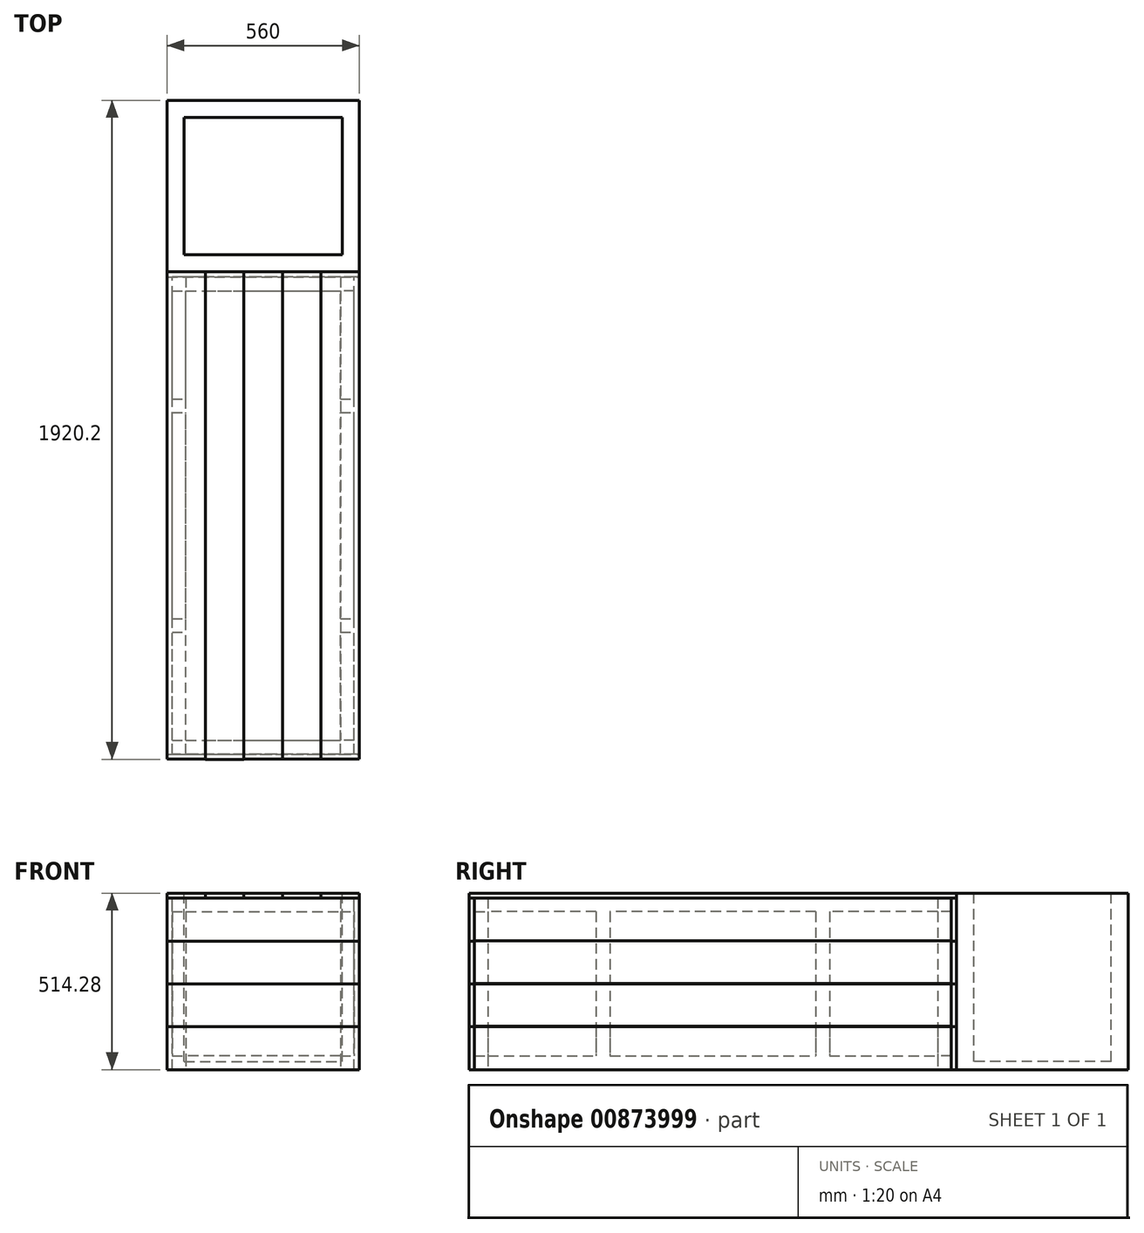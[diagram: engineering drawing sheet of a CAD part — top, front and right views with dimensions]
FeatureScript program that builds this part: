
annotation { "Feature Type Name" : "Feature", "Feature Type Description" : "" }
export const myFeature = defineFeature(function(context is Context, id is Id, definition is map)
    precondition{}
    {
        {
            var Q0;
            Q0=qCreatedBy(makeId("Right.planeOp"),FACE);
            var sketch = newSketch(context, id + "F0", { "sketchPlane" : qUnion([Q0])});
            skLineSegment(sketch, "E0.bottom", {"start": v(0, 0) * mm, "end": v(1390, 0) * mm});
            skLineSegment(sketch, "E0.top", {"start": v(0, 40) * mm, "end": v(1390, 40) * mm});
            skLineSegment(sketch, "E0.left", {"start": v(0, 0) * mm, "end": v(0, 40) * mm});
            skLineSegment(sketch, "E0.right", {"start": v(1390, 0) * mm, "end": v(1390, 40) * mm});
            skSolve(sketch);
        }
        {
            var Q0;
            Q0 = qSketchRegion(id + "F0", true);
            extrude(context, id + "F1", {"entities" : qUnion([Q0]), "depth" : 40 * mm, "offsetDistance" : 25 * mm});
        }
        {
            var Q0;
            Q0=makeQuery(id+"F1.opExtrude","CAP_FACE",FACE,{"disambiguationData":[OSD([sQuery(id+"F0.wireOp",EDGE,"E0.bottom"),sQuery(id+"F0.wireOp",EDGE,"E0.top"),sQuery(id+"F0.wireOp",EDGE,"E0.left"),sQuery(id+"F0.wireOp",EDGE,"E0.right")])],"isStart":true});
            var sketch = newSketch(context, id + "F2", { "sketchPlane" : qUnion([Q0])});
            skLineSegment(sketch, "E1.bottom", {"start": v(-1390, 40) * mm, "end": v(-1350, 40) * mm});
            skLineSegment(sketch, "E1.top", {"start": v(-1390, 0) * mm, "end": v(-1350, 0) * mm});
            skLineSegment(sketch, "E1.left", {"start": v(-1390, 40) * mm, "end": v(-1390, 0) * mm});
            skLineSegment(sketch, "E1.right", {"start": v(-1350, 40) * mm, "end": v(-1350, 0) * mm});
            skLineSegment(sketch, "E2.bottom", {"start": v(0, 40) * mm, "end": v(-40, 40) * mm});
            skLineSegment(sketch, "E2.top", {"start": v(0, 0) * mm, "end": v(-40, 0) * mm});
            skLineSegment(sketch, "E2.left", {"start": v(0, 40) * mm, "end": v(0, 0) * mm});
            skLineSegment(sketch, "E2.right", {"start": v(-40, 40) * mm, "end": v(-40, 0) * mm});
            skSolve(sketch);
        }
        {
            var Q0;
            Q0 = qSketchRegion(id + "F2", true);
            extrude(context, id + "F3", {"entities" : qUnion([Q0]), "operationType" : NewBodyOperationType.ADD, "depth" : 490 * mm, "offsetDistance" : 25 * mm});
        }
        {
            var Q0;
            Q0=makeQuery(id+"F3.opExtrude","SWEPT_FACE",FACE,{"disambiguationData":[OSD([sQuery(id+"F2.wireOp",EDGE,"E1.right")])]});
            var sketch = newSketch(context, id + "F4", { "sketchPlane" : qUnion([Q0])});
            skLineSegment(sketch, "E3.bottom", {"start": v(-490, 40) * mm, "end": v(-450, 40) * mm});
            skLineSegment(sketch, "E3.top", {"start": v(-490, 0) * mm, "end": v(-450, 0) * mm});
            skLineSegment(sketch, "E3.left", {"start": v(-490, 40) * mm, "end": v(-490, 0) * mm});
            skLineSegment(sketch, "E3.right", {"start": v(-450, 40) * mm, "end": v(-450, 0) * mm});
            skSolve(sketch);
        }
        {
            var Q0;
            Q0=makeQuery(id+"F4.imprint","IMPRINT",FACE,{"disambiguationData":[TD([[makeQuery(id+"F4.imprint","IMPRINT",EDGE,{"derivedFrom":sQuery(id+"F4.wireOp",EDGE,"E3.bottom")}),-1.0]])]});
            extrude(context, id + "F5", {"entities" : qUnion([Q0]), "operationType" : NewBodyOperationType.ADD, "depth" : 1310 * mm, "offsetDistance" : 25 * mm});
        }
        {
            var Q0;
            Q0=makeQuery(id+"F5.boolean.opBoolean","MERGE",FACE,{"derivedFrom":[makeQuery(id+"F3.boolean.opBoolean","MERGE",FACE,{"derivedFrom":[makeQuery(id+"F1.opExtrude","SWEPT_FACE",FACE,{"disambiguationData":[OSD([sQuery(id+"F0.wireOp",EDGE,"E0.top")])]}),makeQuery(id+"F3.opExtrude","SWEPT_FACE",FACE,{"disambiguationData":[OSD([sQuery(id+"F2.wireOp",EDGE,"E1.bottom")])]}),makeQuery(id+"F3.opExtrude","SWEPT_FACE",FACE,{"disambiguationData":[OSD([sQuery(id+"F2.wireOp",EDGE,"E2.bottom")])]})]}),makeQuery(id+"F5.opExtrude","SWEPT_FACE",FACE,{"disambiguationData":[OSD([sQuery(id+"F4.wireOp",EDGE,"E3.bottom")])]})]});
            var sketch = newSketch(context, id + "F6", { "sketchPlane" : qUnion([Q0])});
            skLineSegment(sketch, "E4.bottom", {"start": v(-490, 1390) * mm, "end": v(-450, 1390) * mm});
            skLineSegment(sketch, "E4.top", {"start": v(-490, 1350) * mm, "end": v(-450, 1350) * mm});
            skLineSegment(sketch, "E4.left", {"start": v(-490, 1390) * mm, "end": v(-490, 1350) * mm});
            skLineSegment(sketch, "E4.right", {"start": v(-450, 1390) * mm, "end": v(-450, 1350) * mm});
            skLineSegment(sketch, "E5.bottom", {"start": v(40, 1390) * mm, "end": v(0, 1390) * mm});
            skLineSegment(sketch, "E5.top", {"start": v(40, 1350) * mm, "end": v(0, 1350) * mm});
            skLineSegment(sketch, "E5.left", {"start": v(40, 1390) * mm, "end": v(40, 1350) * mm});
            skLineSegment(sketch, "E5.right", {"start": v(0, 1390) * mm, "end": v(0, 1350) * mm});
            skLineSegment(sketch, "E6.bottom", {"start": v(40, 0) * mm, "end": v(0, 0) * mm});
            skLineSegment(sketch, "E6.top", {"start": v(40, 40) * mm, "end": v(0, 40) * mm});
            skLineSegment(sketch, "E6.left", {"start": v(40, 0) * mm, "end": v(40, 40) * mm});
            skLineSegment(sketch, "E6.right", {"start": v(0, 0) * mm, "end": v(0, 40) * mm});
            skLineSegment(sketch, "E7.bottom", {"start": v(-490, 0) * mm, "end": v(-450, 0) * mm});
            skLineSegment(sketch, "E7.top", {"start": v(-490, 40) * mm, "end": v(-450, 40) * mm});
            skLineSegment(sketch, "E7.left", {"start": v(-490, 0) * mm, "end": v(-490, 40) * mm});
            skLineSegment(sketch, "E7.right", {"start": v(-450, 0) * mm, "end": v(-450, 40) * mm});
            skSolve(sketch);
        }
        {
            var Q0;
            Q0 = qSketchRegion(id + "F6", true);
            extrude(context, id + "F7", {"entities" : qUnion([Q0]), "operationType" : NewBodyOperationType.ADD, "depth" : 420 * mm, "offsetDistance" : 25 * mm});
        }
        {
            var Q0;
            Q0=makeQuery(id+"F7.opExtrude","CAP_FACE",FACE,{"disambiguationData":[OSD([sQuery(id+"F6.wireOp",EDGE,"E4.bottom"),sQuery(id+"F6.wireOp",EDGE,"E4.top"),sQuery(id+"F6.wireOp",EDGE,"E4.left"),sQuery(id+"F6.wireOp",EDGE,"E4.right")])],"isStart":false});
            var sketch = newSketch(context, id + "F8", { "sketchPlane" : qUnion([Q0])});
            skLineSegment(sketch, "E8.bottom", {"start": v(-490, 1390) * mm, "end": v(40, 1390) * mm});
            skLineSegment(sketch, "E8.top", {"start": v(-490, 0) * mm, "end": v(40, 0) * mm});
            skLineSegment(sketch, "E8.left", {"start": v(-490, 1390) * mm, "end": v(-490, 0) * mm});
            skLineSegment(sketch, "E8.right", {"start": v(40, 1390) * mm, "end": v(40, 0) * mm});
            skLineSegment(sketch, "E9.bottom", {"start": v(-450, 1350) * mm, "end": v(0, 1350) * mm});
            skLineSegment(sketch, "E9.top", {"start": v(-450, 40) * mm, "end": v(0, 40) * mm});
            skLineSegment(sketch, "E9.left", {"start": v(-450, 1350) * mm, "end": v(-450, 40) * mm});
            skLineSegment(sketch, "E9.right", {"start": v(0, 1350) * mm, "end": v(0, 40) * mm});
            skSolve(sketch);
        }
        {
            var Q0;
            Q0 = qSketchRegion(id + "F8", true);
            extrude(context, id + "F9", {"entities" : qUnion([Q0]), "operationType" : NewBodyOperationType.ADD, "depth" : 40 * mm, "offsetDistance" : 25 * mm});
        }
        {
            var Q0;
            {var subQ1=sQuery(id+"F2.wireOp",EDGE,"E2.bottom");var subQ2=makeQuery(id+"F3.opExtrude","SWEPT_FACE",FACE,{"disambiguationData":[OSD([subQ1])]});var subQ3=sQuery(id+"F2.wireOp",EDGE,"E1.bottom");var subQ4=makeQuery(id+"F3.opExtrude","SWEPT_FACE",FACE,{"disambiguationData":[OSD([subQ3])]});var subQ5=makeQuery(id+"F5.opExtrude","SWEPT_FACE",FACE,{"disambiguationData":[OSD([sQuery(id+"F4.wireOp",EDGE,"E3.bottom")])]});var subQ7=makeQuery(id+"F1.opExtrude","SWEPT_FACE",FACE,{"disambiguationData":[OSD([sQuery(id+"F0.wireOp",EDGE,"E0.top")])]});Q0=makeQuery(id+"F7.boolean.opBoolean","SPLIT",FACE,{"disambiguationData":[TD([makeQuery(id+"F5.opExtrude","SWEPT_FACE",FACE,{"disambiguationData":[OSD([sQuery(id+"F4.wireOp",EDGE,"E3.left")])]})])],"derivedFrom":makeQuery(id+"F5.boolean.opBoolean","MERGE",FACE,{"derivedFrom":[makeQuery(id+"F3.boolean.opBoolean","MERGE",FACE,{"derivedFrom":[subQ7,subQ4,subQ2]}),subQ5]})});}
            var sketch = newSketch(context, id + "F10", { "sketchPlane" : qUnion([Q0])});
            skLineSegment(sketch, "E10", {"start": v(-490, 695) * mm, "end": v(200.64, 695) * mm, "construction": true});
            skLineSegment(sketch, "E11.bottom", {"start": v(-490, 1035) * mm, "end": v(-450, 1035) * mm});
            skLineSegment(sketch, "E11.top", {"start": v(-490, 995) * mm, "end": v(-450, 995) * mm});
            skLineSegment(sketch, "E11.left", {"start": v(-490, 1035) * mm, "end": v(-490, 995) * mm});
            skLineSegment(sketch, "E11.right", {"start": v(-450, 1035) * mm, "end": v(-450, 995) * mm});
            skLineSegment(sketch, "E12.bottom", {"start": v(-490, 395) * mm, "end": v(-450, 395) * mm});
            skLineSegment(sketch, "E12.top", {"start": v(-490, 355) * mm, "end": v(-450, 355) * mm});
            skLineSegment(sketch, "E12.left", {"start": v(-490, 395) * mm, "end": v(-490, 355) * mm});
            skLineSegment(sketch, "E12.right", {"start": v(-450, 395) * mm, "end": v(-450, 355) * mm});
            skSolve(sketch);
        }
        {
            var Q0;
            Q0 = qSketchRegion(id + "F10", true);
            extrude(context, id + "F11", {"entities" : qUnion([Q0]), "operationType" : NewBodyOperationType.ADD, "depth" : 420 * mm, "offsetDistance" : 25 * mm});
        }
        {
            var Q0;
            {var subQ0=makeQuery(id+"F5.opExtrude","SWEPT_FACE",FACE,{"disambiguationData":[OSD([sQuery(id+"F4.wireOp",EDGE,"E3.bottom")])]});var subQ1=makeQuery(id+"F3.opExtrude","SWEPT_FACE",FACE,{"disambiguationData":[OSD([sQuery(id+"F2.wireOp",EDGE,"E2.bottom")])]});var subQ4=sQuery(id+"F0.wireOp",EDGE,"E0.top");var subQ6=makeQuery(id+"F1.opExtrude","SWEPT_FACE",FACE,{"disambiguationData":[OSD([subQ4])]});var subQ7=makeQuery(id+"F3.opExtrude","SWEPT_FACE",FACE,{"disambiguationData":[OSD([sQuery(id+"F2.wireOp",EDGE,"E1.bottom")])]});Q0=makeQuery(id+"F7.boolean.opBoolean","SPLIT",FACE,{"disambiguationData":[TD([makeQuery(id+"F7.opExtrude","SWEPT_FACE",FACE,{"disambiguationData":[OSD([sQuery(id+"F6.wireOp",EDGE,"E5.left")])]})])],"derivedFrom":makeQuery(id+"F5.boolean.opBoolean","MERGE",FACE,{"derivedFrom":[makeQuery(id+"F3.boolean.opBoolean","MERGE",FACE,{"derivedFrom":[subQ6,subQ7,subQ1]}),subQ0]})});}
            var sketch = newSketch(context, id + "F12", { "sketchPlane" : qUnion([Q0])});
            skLineSegment(sketch, "E13", {"start": v(40, 695) * mm, "end": v(-725.04, 695) * mm, "construction": true});
            skLineSegment(sketch, "E14.bottom", {"start": v(0, 1035) * mm, "end": v(40, 1035) * mm});
            skLineSegment(sketch, "E14.top", {"start": v(0, 995) * mm, "end": v(40, 995) * mm});
            skLineSegment(sketch, "E14.left", {"start": v(0, 1035) * mm, "end": v(0, 995) * mm});
            skLineSegment(sketch, "E14.right", {"start": v(40, 1035) * mm, "end": v(40, 995) * mm});
            skLineSegment(sketch, "E15.bottom", {"start": v(0, 395) * mm, "end": v(40, 395) * mm});
            skLineSegment(sketch, "E15.top", {"start": v(0, 355) * mm, "end": v(40, 355) * mm});
            skLineSegment(sketch, "E15.left", {"start": v(0, 395) * mm, "end": v(0, 355) * mm});
            skLineSegment(sketch, "E15.right", {"start": v(40, 395) * mm, "end": v(40, 355) * mm});
            skSolve(sketch);
        }
        {
            var Q0;
            Q0 = qSketchRegion(id + "F12", true);
            extrude(context, id + "F13", {"entities" : qUnion([Q0]), "operationType" : NewBodyOperationType.ADD, "depth" : 420 * mm, "offsetDistance" : 25 * mm});
        }
        {
            var Q0;
            Q0=makeQuery(id+"F11.boolean.opBoolean","MERGE",FACE,{"derivedFrom":[makeQuery(id+"F9.boolean.opBoolean","MERGE",FACE,{"derivedFrom":[makeQuery(id+"F7.boolean.opBoolean","MERGE",FACE,{"derivedFrom":[makeQuery(id+"F5.boolean.opBoolean","MERGE",FACE,{"derivedFrom":[makeQuery(id+"F3.opExtrude","CAP_FACE",FACE,{"disambiguationData":[OSD([sQuery(id+"F2.wireOp",EDGE,"E1.bottom"),sQuery(id+"F2.wireOp",EDGE,"E1.top"),sQuery(id+"F2.wireOp",EDGE,"E1.left"),sQuery(id+"F2.wireOp",EDGE,"E1.right")])],"isStart":false}),makeQuery(id+"F3.opExtrude","CAP_FACE",FACE,{"disambiguationData":[OSD([sQuery(id+"F2.wireOp",EDGE,"E2.bottom"),sQuery(id+"F2.wireOp",EDGE,"E2.top"),sQuery(id+"F2.wireOp",EDGE,"E2.left"),sQuery(id+"F2.wireOp",EDGE,"E2.right")])],"isStart":false}),makeQuery(id+"F5.opExtrude","SWEPT_FACE",FACE,{"disambiguationData":[OSD([sQuery(id+"F4.wireOp",EDGE,"E3.left")])]})]}),makeQuery(id+"F7.opExtrude","SWEPT_FACE",FACE,{"disambiguationData":[OSD([sQuery(id+"F6.wireOp",EDGE,"E4.left")])]}),makeQuery(id+"F7.opExtrude","SWEPT_FACE",FACE,{"disambiguationData":[OSD([sQuery(id+"F6.wireOp",EDGE,"E7.left")])]})]}),makeQuery(id+"F9.opExtrude","SWEPT_FACE",FACE,{"disambiguationData":[OSD([sQuery(id+"F8.wireOp",EDGE,"E8.left")])]})]}),makeQuery(id+"F11.opExtrude","SWEPT_FACE",FACE,{"disambiguationData":[OSD([sQuery(id+"F10.wireOp",EDGE,"E11.left")])]}),makeQuery(id+"F11.opExtrude","SWEPT_FACE",FACE,{"disambiguationData":[OSD([sQuery(id+"F10.wireOp",EDGE,"E12.left")])]})]});
            var sketch = newSketch(context, id + "F14", { "sketchPlane" : qUnion([Q0])});
            skSolve(sketch);
        }
        {
            var Q0;
            Q0=makeQuery(id+"F13.boolean.opBoolean","MERGE",FACE,{"derivedFrom":[makeQuery(id+"F9.boolean.opBoolean","MERGE",FACE,{"derivedFrom":[makeQuery(id+"F7.boolean.opBoolean","MERGE",FACE,{"derivedFrom":[makeQuery(id+"F1.opExtrude","CAP_FACE",FACE,{"disambiguationData":[OSD([sQuery(id+"F0.wireOp",EDGE,"E0.bottom"),sQuery(id+"F0.wireOp",EDGE,"E0.top"),sQuery(id+"F0.wireOp",EDGE,"E0.left"),sQuery(id+"F0.wireOp",EDGE,"E0.right")])],"isStart":false}),makeQuery(id+"F7.opExtrude","SWEPT_FACE",FACE,{"disambiguationData":[OSD([sQuery(id+"F6.wireOp",EDGE,"E5.left")])]}),makeQuery(id+"F7.opExtrude","SWEPT_FACE",FACE,{"disambiguationData":[OSD([sQuery(id+"F6.wireOp",EDGE,"E6.left")])]})]}),makeQuery(id+"F9.opExtrude","SWEPT_FACE",FACE,{"disambiguationData":[OSD([sQuery(id+"F8.wireOp",EDGE,"E8.right")])]})]}),makeQuery(id+"F13.opExtrude","SWEPT_FACE",FACE,{"disambiguationData":[OSD([sQuery(id+"F12.wireOp",EDGE,"E14.right")])]}),makeQuery(id+"F13.opExtrude","SWEPT_FACE",FACE,{"disambiguationData":[OSD([sQuery(id+"F12.wireOp",EDGE,"E15.right")])]})]});
            var sketch = newSketch(context, id + "F15", { "sketchPlane" : qUnion([Q0])});
            skLineSegment(sketch, "E16.bottom", {"start": v(0, 500) * mm, "end": v(1390, 500) * mm});
            skLineSegment(sketch, "E16.top", {"start": v(0, 375) * mm, "end": v(1390, 375) * mm});
            skLineSegment(sketch, "E16.left", {"start": v(0, 500) * mm, "end": v(0, 375) * mm});
            skLineSegment(sketch, "E16.right", {"start": v(1390, 500) * mm, "end": v(1390, 375) * mm});
            skSolve(sketch);
        }
        {
            var Q0;
            Q0 = qSketchRegion(id + "F15", true);
            extrude(context, id + "F16", {"entities" : qUnion([Q0]), "depth" : 15 * mm, "offsetDistance" : 25 * mm});
        }
        {
            var Q0;
            Q0=makeQuery(id+"F13.boolean.opBoolean","MERGE",FACE,{"derivedFrom":[makeQuery(id+"F9.boolean.opBoolean","MERGE",FACE,{"derivedFrom":[makeQuery(id+"F7.boolean.opBoolean","MERGE",FACE,{"derivedFrom":[makeQuery(id+"F1.opExtrude","CAP_FACE",FACE,{"disambiguationData":[OSD([sQuery(id+"F0.wireOp",EDGE,"E0.bottom"),sQuery(id+"F0.wireOp",EDGE,"E0.top"),sQuery(id+"F0.wireOp",EDGE,"E0.left"),sQuery(id+"F0.wireOp",EDGE,"E0.right")])],"isStart":false}),makeQuery(id+"F7.opExtrude","SWEPT_FACE",FACE,{"disambiguationData":[OSD([sQuery(id+"F6.wireOp",EDGE,"E5.left")])]}),makeQuery(id+"F7.opExtrude","SWEPT_FACE",FACE,{"disambiguationData":[OSD([sQuery(id+"F6.wireOp",EDGE,"E6.left")])]})]}),makeQuery(id+"F9.opExtrude","SWEPT_FACE",FACE,{"disambiguationData":[OSD([sQuery(id+"F8.wireOp",EDGE,"E8.right")])]})]}),makeQuery(id+"F13.opExtrude","SWEPT_FACE",FACE,{"disambiguationData":[OSD([sQuery(id+"F12.wireOp",EDGE,"E14.right")])]}),makeQuery(id+"F13.opExtrude","SWEPT_FACE",FACE,{"disambiguationData":[OSD([sQuery(id+"F12.wireOp",EDGE,"E15.right")])]})]});
            var sketch = newSketch(context, id + "F17", { "sketchPlane" : qUnion([Q0])});
            skLineSegment(sketch, "E17.bottom", {"start": v(0, 0) * mm, "end": v(1390, 0) * mm});
            skLineSegment(sketch, "E17.top", {"start": v(0, 125) * mm, "end": v(1390, 125) * mm});
            skLineSegment(sketch, "E17.left", {"start": v(0, 0) * mm, "end": v(0, 125) * mm});
            skLineSegment(sketch, "E17.right", {"start": v(1390, 0) * mm, "end": v(1390, 125) * mm});
            skSolve(sketch);
        }
        {
            var Q0;
            Q0 = qSketchRegion(id + "F17", true);
            extrude(context, id + "F18", {"entities" : qUnion([Q0]), "depth" : 15 * mm, "offsetDistance" : 25 * mm});
        }
        {
            var Q0;
            Q0=makeQuery(id+"F13.boolean.opBoolean","MERGE",FACE,{"derivedFrom":[makeQuery(id+"F9.boolean.opBoolean","MERGE",FACE,{"derivedFrom":[makeQuery(id+"F7.boolean.opBoolean","MERGE",FACE,{"derivedFrom":[makeQuery(id+"F1.opExtrude","CAP_FACE",FACE,{"disambiguationData":[OSD([sQuery(id+"F0.wireOp",EDGE,"E0.bottom"),sQuery(id+"F0.wireOp",EDGE,"E0.top"),sQuery(id+"F0.wireOp",EDGE,"E0.left"),sQuery(id+"F0.wireOp",EDGE,"E0.right")])],"isStart":false}),makeQuery(id+"F7.opExtrude","SWEPT_FACE",FACE,{"disambiguationData":[OSD([sQuery(id+"F6.wireOp",EDGE,"E5.left")])]}),makeQuery(id+"F7.opExtrude","SWEPT_FACE",FACE,{"disambiguationData":[OSD([sQuery(id+"F6.wireOp",EDGE,"E6.left")])]})]}),makeQuery(id+"F9.opExtrude","SWEPT_FACE",FACE,{"disambiguationData":[OSD([sQuery(id+"F8.wireOp",EDGE,"E8.right")])]})]}),makeQuery(id+"F13.opExtrude","SWEPT_FACE",FACE,{"disambiguationData":[OSD([sQuery(id+"F12.wireOp",EDGE,"E14.right")])]}),makeQuery(id+"F13.opExtrude","SWEPT_FACE",FACE,{"disambiguationData":[OSD([sQuery(id+"F12.wireOp",EDGE,"E15.right")])]})]});
            var sketch = newSketch(context, id + "F19", { "sketchPlane" : qUnion([Q0])});
            skLineSegment(sketch, "E18.bottom", {"start": v(0, 251.2) * mm, "end": v(1390, 251.2) * mm});
            skLineSegment(sketch, "E18.top", {"start": v(0, 126.2) * mm, "end": v(1390, 126.2) * mm});
            skLineSegment(sketch, "E18.left", {"start": v(0, 251.2) * mm, "end": v(0, 126.2) * mm});
            skLineSegment(sketch, "E18.right", {"start": v(1390, 251.2) * mm, "end": v(1390, 126.2) * mm});
            skSolve(sketch);
        }
        {
            var Q0;
            Q0 = qSketchRegion(id + "F19", true);
            extrude(context, id + "F20", {"entities" : qUnion([Q0]), "depth" : 15 * mm, "offsetDistance" : 25 * mm});
        }
        {
            var Q0;
            Q0=makeQuery(id+"F13.boolean.opBoolean","MERGE",FACE,{"derivedFrom":[makeQuery(id+"F9.boolean.opBoolean","MERGE",FACE,{"derivedFrom":[makeQuery(id+"F7.boolean.opBoolean","MERGE",FACE,{"derivedFrom":[makeQuery(id+"F1.opExtrude","CAP_FACE",FACE,{"disambiguationData":[OSD([sQuery(id+"F0.wireOp",EDGE,"E0.bottom"),sQuery(id+"F0.wireOp",EDGE,"E0.top"),sQuery(id+"F0.wireOp",EDGE,"E0.left"),sQuery(id+"F0.wireOp",EDGE,"E0.right")])],"isStart":false}),makeQuery(id+"F7.opExtrude","SWEPT_FACE",FACE,{"disambiguationData":[OSD([sQuery(id+"F6.wireOp",EDGE,"E5.left")])]}),makeQuery(id+"F7.opExtrude","SWEPT_FACE",FACE,{"disambiguationData":[OSD([sQuery(id+"F6.wireOp",EDGE,"E6.left")])]})]}),makeQuery(id+"F9.opExtrude","SWEPT_FACE",FACE,{"disambiguationData":[OSD([sQuery(id+"F8.wireOp",EDGE,"E8.right")])]})]}),makeQuery(id+"F13.opExtrude","SWEPT_FACE",FACE,{"disambiguationData":[OSD([sQuery(id+"F12.wireOp",EDGE,"E14.right")])]}),makeQuery(id+"F13.opExtrude","SWEPT_FACE",FACE,{"disambiguationData":[OSD([sQuery(id+"F12.wireOp",EDGE,"E15.right")])]})]});
            var sketch = newSketch(context, id + "F21", { "sketchPlane" : qUnion([Q0])});
            skLineSegment(sketch, "E19.bottom", {"start": v(0, 250) * mm, "end": v(1390, 250) * mm});
            skLineSegment(sketch, "E19.top", {"start": v(0, 375) * mm, "end": v(1390, 375) * mm});
            skLineSegment(sketch, "E19.left", {"start": v(0, 250) * mm, "end": v(0, 375) * mm});
            skLineSegment(sketch, "E19.right", {"start": v(1390, 250) * mm, "end": v(1390, 375) * mm});
            skSolve(sketch);
        }
        {
            var Q0;
            Q0 = qSketchRegion(id + "F21", true);
            extrude(context, id + "F22", {"entities" : qUnion([Q0]), "depth" : 15 * mm, "offsetDistance" : 25 * mm});
        }
        {
            var Q0;
            {var subQ10=sQuery(id+"F8.wireOp",EDGE,"E8.left");Q0=makeQuery(id+"F14.imprint","IMPRINT",FACE,{"disambiguationData":[TD([[makeQuery(id+"F14.imprint","IMPRINT",EDGE,{"derivedFrom":makeQuery(id+"F9.opExtrude","CAP_EDGE",EDGE,{"disambiguationData":[OSD([subQ10])],"isStart":false})}),1.0]])]});}
            var sketch = newSketch(context, id + "F23", { "sketchPlane" : qUnion([Q0])});
            skLineSegment(sketch, "E20.bottom", {"start": v(0, 0) * mm, "end": v(-1390, 0) * mm});
            skLineSegment(sketch, "E20.top", {"start": v(0, 125) * mm, "end": v(-1390, 125) * mm});
            skLineSegment(sketch, "E20.left", {"start": v(0, 0) * mm, "end": v(0, 125) * mm});
            skLineSegment(sketch, "E20.right", {"start": v(-1390, 0) * mm, "end": v(-1390, 125) * mm});
            skSolve(sketch);
        }
        {
            var Q0;
            Q0 = qSketchRegion(id + "F23", true);
            extrude(context, id + "F24", {"entities" : qUnion([Q0]), "depth" : 15 * mm, "offsetDistance" : 25 * mm});
        }
        {
            var Q0;
            {var subQ10=sQuery(id+"F8.wireOp",EDGE,"E8.left");Q0=makeQuery(id+"F14.imprint","IMPRINT",FACE,{"disambiguationData":[TD([[makeQuery(id+"F14.imprint","IMPRINT",EDGE,{"derivedFrom":makeQuery(id+"F9.opExtrude","CAP_EDGE",EDGE,{"disambiguationData":[OSD([subQ10])],"isStart":false})}),1.0]])]});}
            var sketch = newSketch(context, id + "F25", { "sketchPlane" : qUnion([Q0])});
            skLineSegment(sketch, "E21.bottom", {"start": v(0, 124.95) * mm, "end": v(-1390, 124.95) * mm});
            skLineSegment(sketch, "E21.top", {"start": v(0, 250) * mm, "end": v(-1390, 250) * mm});
            skLineSegment(sketch, "E21.left", {"start": v(0, 124.95) * mm, "end": v(0, 250) * mm});
            skLineSegment(sketch, "E21.right", {"start": v(-1390, 124.95) * mm, "end": v(-1390, 250) * mm});
            skSolve(sketch);
        }
        {
            var Q0;
            Q0 = qSketchRegion(id + "F25", true);
            extrude(context, id + "F26", {"entities" : qUnion([Q0]), "depth" : 15 * mm, "offsetDistance" : 25 * mm});
        }
        {
            var Q0;
            {var subQ10=sQuery(id+"F8.wireOp",EDGE,"E8.left");Q0=makeQuery(id+"F14.imprint","IMPRINT",FACE,{"disambiguationData":[TD([[makeQuery(id+"F14.imprint","IMPRINT",EDGE,{"derivedFrom":makeQuery(id+"F9.opExtrude","CAP_EDGE",EDGE,{"disambiguationData":[OSD([subQ10])],"isStart":false})}),1.0]])]});}
            var sketch = newSketch(context, id + "F27", { "sketchPlane" : qUnion([Q0])});
            skLineSegment(sketch, "E22.bottom", {"start": v(0, 249.73) * mm, "end": v(-1390, 249.73) * mm});
            skLineSegment(sketch, "E22.top", {"start": v(0, 374.73) * mm, "end": v(-1390, 374.73) * mm});
            skLineSegment(sketch, "E22.left", {"start": v(0, 249.73) * mm, "end": v(0, 374.73) * mm});
            skLineSegment(sketch, "E22.right", {"start": v(-1390, 249.73) * mm, "end": v(-1390, 374.73) * mm});
            skSolve(sketch);
        }
        {
            var Q0;
            Q0 = qSketchRegion(id + "F27", true);
            extrude(context, id + "F28", {"entities" : qUnion([Q0]), "depth" : 15 * mm, "offsetDistance" : 25 * mm});
        }
        {
            var Q0;
            {var subQ10=sQuery(id+"F8.wireOp",EDGE,"E8.left");Q0=makeQuery(id+"F14.imprint","IMPRINT",FACE,{"disambiguationData":[TD([[makeQuery(id+"F14.imprint","IMPRINT",EDGE,{"derivedFrom":makeQuery(id+"F9.opExtrude","CAP_EDGE",EDGE,{"disambiguationData":[OSD([subQ10])],"isStart":false})}),1.0]])]});}
            var sketch = newSketch(context, id + "F29", { "sketchPlane" : qUnion([Q0])});
            skLineSegment(sketch, "E23.bottom", {"start": v(0, 374.28) * mm, "end": v(-1390, 374.28) * mm});
            skLineSegment(sketch, "E23.top", {"start": v(0, 499.28) * mm, "end": v(-1390, 499.28) * mm});
            skLineSegment(sketch, "E23.left", {"start": v(0, 374.28) * mm, "end": v(0, 499.28) * mm});
            skLineSegment(sketch, "E23.right", {"start": v(-1390, 374.28) * mm, "end": v(-1390, 499.28) * mm});
            skSolve(sketch);
        }
        {
            var Q0;
            Q0 = qSketchRegion(id + "F29", true);
            extrude(context, id + "F30", {"entities" : qUnion([Q0]), "depth" : 15 * mm, "offsetDistance" : 25 * mm});
        }
        {
            var Q0;
            Q0=makeQuery(id+"F9.boolean.opBoolean","MERGE",FACE,{"derivedFrom":[makeQuery(id+"F7.boolean.opBoolean","MERGE",FACE,{"derivedFrom":[makeQuery(id+"F3.boolean.opBoolean","MERGE",FACE,{"derivedFrom":[makeQuery(id+"F1.opExtrude","SWEPT_FACE",FACE,{"disambiguationData":[OSD([sQuery(id+"F0.wireOp",EDGE,"E0.left")])]}),makeQuery(id+"F3.opExtrude","SWEPT_FACE",FACE,{"disambiguationData":[OSD([sQuery(id+"F2.wireOp",EDGE,"E2.left")])]})]}),makeQuery(id+"F7.opExtrude","SWEPT_FACE",FACE,{"disambiguationData":[OSD([sQuery(id+"F6.wireOp",EDGE,"E6.bottom")])]}),makeQuery(id+"F7.opExtrude","SWEPT_FACE",FACE,{"disambiguationData":[OSD([sQuery(id+"F6.wireOp",EDGE,"E7.bottom")])]})]}),makeQuery(id+"F9.opExtrude","SWEPT_FACE",FACE,{"disambiguationData":[OSD([sQuery(id+"F8.wireOp",EDGE,"E8.top")])]})]});
            cPlane(context, id + "F31", {"entities" : qUnion([Q0]), "cplaneType" : CPlaneType.OFFSET, "offset" : 695 * mm, "oppositeDirection" : true, "width" : 150 * mm, "height" : 150 * mm});
        }
        {
            var Q0;
            Q0=makeQuery(id+"F24.opExtrude","SWEPT_FACE",FACE,{"disambiguationData":[OSD([sQuery(id+"F23.wireOp",EDGE,"E20.left")])]});
            var sketch = newSketch(context, id + "F32", { "sketchPlane" : qUnion([Q0])});
            skLineSegment(sketch, "E24.bottom", {"start": v(-505, 0) * mm, "end": v(55, 0) * mm});
            skLineSegment(sketch, "E24.top", {"start": v(-505, 125) * mm, "end": v(55, 125) * mm});
            skLineSegment(sketch, "E24.left", {"start": v(-505, 0) * mm, "end": v(-505, 125) * mm});
            skLineSegment(sketch, "E24.right", {"start": v(55, 0) * mm, "end": v(55, 125) * mm});
            skSolve(sketch);
        }
        {
            var Q0;
            Q0 = qSketchRegion(id + "F32", true);
            extrude(context, id + "F33", {"entities" : qUnion([Q0]), "depth" : 15 * mm, "offsetDistance" : 25 * mm});
        }
        {
            var Q0;
            Q0=makeQuery(id+"F26.opExtrude","SWEPT_FACE",FACE,{"disambiguationData":[OSD([sQuery(id+"F25.wireOp",EDGE,"E21.left")])]});
            var sketch = newSketch(context, id + "F34", { "sketchPlane" : qUnion([Q0])});
            skLineSegment(sketch, "E25.bottom", {"start": v(-505, 124.95) * mm, "end": v(55, 124.95) * mm});
            skLineSegment(sketch, "E25.top", {"start": v(-505, 249.95) * mm, "end": v(55, 249.95) * mm});
            skLineSegment(sketch, "E25.left", {"start": v(-505, 124.95) * mm, "end": v(-505, 249.95) * mm});
            skLineSegment(sketch, "E25.right", {"start": v(55, 124.95) * mm, "end": v(55, 249.95) * mm});
            skSolve(sketch);
        }
        {
            var Q0;
            Q0 = qSketchRegion(id + "F34", true);
            extrude(context, id + "F35", {"entities" : qUnion([Q0]), "depth" : 15 * mm, "offsetDistance" : 25 * mm});
        }
        {
            var Q0;
            Q0=makeQuery(id+"F28.opExtrude","SWEPT_FACE",FACE,{"disambiguationData":[OSD([sQuery(id+"F27.wireOp",EDGE,"E22.left")])]});
            var sketch = newSketch(context, id + "F36", { "sketchPlane" : qUnion([Q0])});
            skLineSegment(sketch, "E26.bottom", {"start": v(-505, 249.73) * mm, "end": v(55, 249.73) * mm});
            skLineSegment(sketch, "E26.top", {"start": v(-505, 374.73) * mm, "end": v(55, 374.73) * mm});
            skLineSegment(sketch, "E26.left", {"start": v(-505, 249.73) * mm, "end": v(-505, 374.73) * mm});
            skLineSegment(sketch, "E26.right", {"start": v(55, 249.73) * mm, "end": v(55, 374.73) * mm});
            skSolve(sketch);
        }
        {
            var Q0;
            Q0 = qSketchRegion(id + "F36", true);
            extrude(context, id + "F37", {"entities" : qUnion([Q0]), "depth" : 15 * mm, "offsetDistance" : 25 * mm});
        }
        {
            var Q0;
            Q0=makeQuery(id+"F30.opExtrude","SWEPT_FACE",FACE,{"disambiguationData":[OSD([sQuery(id+"F29.wireOp",EDGE,"E23.left")])]});
            var sketch = newSketch(context, id + "F38", { "sketchPlane" : qUnion([Q0])});
            skLineSegment(sketch, "E27.bottom", {"start": v(-505, 374.28) * mm, "end": v(55, 374.28) * mm});
            skLineSegment(sketch, "E27.top", {"start": v(-505, 499.28) * mm, "end": v(55, 499.28) * mm});
            skLineSegment(sketch, "E27.left", {"start": v(-505, 374.28) * mm, "end": v(-505, 499.28) * mm});
            skLineSegment(sketch, "E27.right", {"start": v(55, 374.28) * mm, "end": v(55, 499.28) * mm});
            skSolve(sketch);
        }
        {
            var Q0;
            Q0 = qSketchRegion(id + "F38", true);
            extrude(context, id + "F39", {"entities" : qUnion([Q0]), "depth" : 15 * mm, "offsetDistance" : 25 * mm});
        }
        {
            var Q0;
            Q0=makeQuery(id+"F39.opExtrude","SWEPT_BODY",BODY,{"disambiguationData":[OSD([sQuery(id+"F38.wireOp",EDGE,"E27.bottom"),sQuery(id+"F38.wireOp",EDGE,"E27.top"),sQuery(id+"F38.wireOp",EDGE,"E27.left"),sQuery(id+"F38.wireOp",EDGE,"E27.right")])]});
            var Q1;
            Q1=makeQuery(id+"F37.opExtrude","SWEPT_BODY",BODY,{"disambiguationData":[OSD([sQuery(id+"F36.wireOp",EDGE,"E26.bottom"),sQuery(id+"F36.wireOp",EDGE,"E26.top"),sQuery(id+"F36.wireOp",EDGE,"E26.left"),sQuery(id+"F36.wireOp",EDGE,"E26.right")])]});
            var Q2;
            Q2=makeQuery(id+"F35.opExtrude","SWEPT_BODY",BODY,{"disambiguationData":[OSD([sQuery(id+"F34.wireOp",EDGE,"E25.bottom"),sQuery(id+"F34.wireOp",EDGE,"E25.top"),sQuery(id+"F34.wireOp",EDGE,"E25.left"),sQuery(id+"F34.wireOp",EDGE,"E25.right")])]});
            var Q3;
            Q3=makeQuery(id+"F33.opExtrude","SWEPT_BODY",BODY,{"disambiguationData":[OSD([sQuery(id+"F32.wireOp",EDGE,"E24.bottom"),sQuery(id+"F32.wireOp",EDGE,"E24.top"),sQuery(id+"F32.wireOp",EDGE,"E24.left"),sQuery(id+"F32.wireOp",EDGE,"E24.right")])]});
            var Q4;
            Q4=qCreatedBy(id+"F31.planeOp",FACE);
            mirror(context, id + "F40", {"entities" : qUnion([Q0, Q1, Q2, Q3]), "mirrorPlane" : qUnion([Q4])});
        }
        {
            var Q0;
            Q0=makeQuery(id+"F9.opExtrude","CAP_FACE",FACE,{"disambiguationData":[OSD([sQuery(id+"F8.wireOp",EDGE,"E8.bottom"),sQuery(id+"F8.wireOp",EDGE,"E8.top"),sQuery(id+"F8.wireOp",EDGE,"E8.left"),sQuery(id+"F8.wireOp",EDGE,"E8.right"),sQuery(id+"F8.wireOp",EDGE,"E9.bottom"),sQuery(id+"F8.wireOp",EDGE,"E9.top"),sQuery(id+"F8.wireOp",EDGE,"E9.left"),sQuery(id+"F8.wireOp",EDGE,"E9.right")])],"isStart":false});
            var sketch = newSketch(context, id + "F41", { "sketchPlane" : qUnion([Q0])});
            skSolve(sketch);
        }
        {
            var Q0;
            Q0=makeQuery(id+"F40.opPattern","COPY",FACE,{"derivedFrom":makeQuery(id+"F39.opExtrude","SWEPT_FACE",FACE,{"disambiguationData":[OSD([sQuery(id+"F38.wireOp",EDGE,"E27.top")])]}),"instanceName":"1"});
            var sketch = newSketch(context, id + "F42", { "sketchPlane" : qUnion([Q0])});
            skLineSegment(sketch, "E28.bottom", {"start": v(-505, 1405) * mm, "end": v(-393, 1405) * mm});
            skLineSegment(sketch, "E28.top", {"start": v(-505, -15) * mm, "end": v(-393, -15) * mm});
            skLineSegment(sketch, "E28.left", {"start": v(-505, 1405) * mm, "end": v(-505, -15) * mm});
            skLineSegment(sketch, "E28.right", {"start": v(-393, 1405) * mm, "end": v(-393, -15) * mm});
            skSolve(sketch);
        }
        {
            var Q0;
            Q0 = qSketchRegion(id + "F42", true);
            extrude(context, id + "F43", {"entities" : qUnion([Q0]), "depth" : 14.2 * mm, "offsetDistance" : 25 * mm});
        }
        {
            var Q0;
            Q0=makeQuery(id+"F40.opPattern","COPY",FACE,{"derivedFrom":makeQuery(id+"F39.opExtrude","SWEPT_FACE",FACE,{"disambiguationData":[OSD([sQuery(id+"F38.wireOp",EDGE,"E27.top")])]}),"instanceName":"1"});
            var sketch = newSketch(context, id + "F44", { "sketchPlane" : qUnion([Q0])});
            skLineSegment(sketch, "E29.bottom", {"start": v(55, 1405) * mm, "end": v(-57, 1405) * mm});
            skLineSegment(sketch, "E29.top", {"start": v(55, -15) * mm, "end": v(-57, -15) * mm});
            skLineSegment(sketch, "E29.left", {"start": v(55, 1405) * mm, "end": v(55, -15) * mm});
            skLineSegment(sketch, "E29.right", {"start": v(-57, 1405) * mm, "end": v(-57, -15) * mm});
            skSolve(sketch);
        }
        {
            var Q0;
            Q0 = qSketchRegion(id + "F44", true);
            extrude(context, id + "F45", {"entities" : qUnion([Q0]), "depth" : 15 * mm, "offsetDistance" : 25 * mm});
        }
        {
            var Q0;
            Q0=makeQuery(id+"F40.opPattern","COPY",FACE,{"derivedFrom":makeQuery(id+"F39.opExtrude","SWEPT_FACE",FACE,{"disambiguationData":[OSD([sQuery(id+"F38.wireOp",EDGE,"E27.top")])]}),"instanceName":"1"});
            var sketch = newSketch(context, id + "F46", { "sketchPlane" : qUnion([Q0])});
            skSolve(sketch);
        }
        {
            var Q0;
            Q0=makeQuery(id+"F41.imprint","IMPRINT",FACE,{"disambiguationData":[TD([[makeQuery(id+"F41.imprint","IMPRINT",EDGE,{"derivedFrom":makeQuery(id+"F9.opExtrude","CAP_EDGE",EDGE,{"disambiguationData":[OSD([sQuery(id+"F8.wireOp",EDGE,"E8.bottom")])],"isStart":false})}),1.0]])]});
            var sketch = newSketch(context, id + "F47", { "sketchPlane" : qUnion([Q0])});
            skLineSegment(sketch, "E30.bottom", {"start": v(-392.99, 1404.8) * mm, "end": v(-280.99, 1404.8) * mm});
            skLineSegment(sketch, "E30.top", {"start": v(-392.99, -15.2) * mm, "end": v(-280.99, -15.2) * mm});
            skLineSegment(sketch, "E30.left", {"start": v(-392.99, 1404.8) * mm, "end": v(-392.99, -15.2) * mm});
            skLineSegment(sketch, "E30.right", {"start": v(-280.99, 1404.8) * mm, "end": v(-280.99, -15.2) * mm});
            skSolve(sketch);
        }
        {
            var Q0;
            Q0 = qSketchRegion(id + "F47", true);
            extrude(context, id + "F48", {"entities" : qUnion([Q0]), "operationType" : NewBodyOperationType.ADD, "depth" : 14 * mm, "offsetDistance" : 25 * mm});
        }
        {
            var Q0;
            {var subQ0=sQuery(id+"F38.wireOp",EDGE,"E27.top");Q0=makeQuery(id+"F46.imprint","IMPRINT",FACE,{"disambiguationData":[TD([[makeQuery(id+"F46.imprint","IMPRINT",EDGE,{"derivedFrom":makeQuery(id+"F40.opPattern","COPY",EDGE,{"derivedFrom":makeQuery(id+"F39.opExtrude","CAP_EDGE",EDGE,{"disambiguationData":[OSD([subQ0])],"isStart":true}),"instanceName":"1"})}),1.0]])]});}
            var sketch = newSketch(context, id + "F49", { "sketchPlane" : qUnion([Q0])});
            skLineSegment(sketch, "E31.bottom", {"start": v(-280.99, 1404.96) * mm, "end": v(-168.99, 1404.96) * mm});
            skLineSegment(sketch, "E31.top", {"start": v(-280.99, -15.04) * mm, "end": v(-168.99, -15.04) * mm});
            skLineSegment(sketch, "E31.left", {"start": v(-280.99, 1404.96) * mm, "end": v(-280.99, -15.04) * mm});
            skLineSegment(sketch, "E31.right", {"start": v(-168.99, 1404.96) * mm, "end": v(-168.99, -15.04) * mm});
            skSolve(sketch);
        }
        {
            var Q0;
            Q0 = qSketchRegion(id + "F49", true);
            extrude(context, id + "F50", {"entities" : qUnion([Q0]), "depth" : 15 * mm, "offsetDistance" : 25 * mm});
        }
        {
            var Q0;
            {var subQ0=sQuery(id+"F38.wireOp",EDGE,"E27.top");Q0=makeQuery(id+"F46.imprint","IMPRINT",FACE,{"disambiguationData":[TD([[makeQuery(id+"F46.imprint","IMPRINT",EDGE,{"derivedFrom":makeQuery(id+"F40.opPattern","COPY",EDGE,{"derivedFrom":makeQuery(id+"F39.opExtrude","CAP_EDGE",EDGE,{"disambiguationData":[OSD([subQ0])],"isStart":true}),"instanceName":"1"})}),1.0]])]});}
            var sketch = newSketch(context, id + "F51", { "sketchPlane" : qUnion([Q0])});
            skLineSegment(sketch, "E32.bottom", {"start": v(-169, 1404.98) * mm, "end": v(-57, 1404.98) * mm});
            skLineSegment(sketch, "E32.top", {"start": v(-169, -15.02) * mm, "end": v(-57, -15.02) * mm});
            skLineSegment(sketch, "E32.left", {"start": v(-169, 1404.98) * mm, "end": v(-169, -15.02) * mm});
            skLineSegment(sketch, "E32.right", {"start": v(-57, 1404.98) * mm, "end": v(-57, -15.02) * mm});
            skSolve(sketch);
        }
        {
            var Q0;
            Q0 = qSketchRegion(id + "F51", true);
            extrude(context, id + "F52", {"entities" : qUnion([Q0]), "depth" : 15 * mm, "offsetDistance" : 25 * mm});
        }
        {
            var Q0;
            Q0=makeQuery(id+"F40.opPattern","COPY",FACE,{"derivedFrom":makeQuery(id+"F33.opExtrude","SWEPT_FACE",FACE,{"disambiguationData":[OSD([sQuery(id+"F32.wireOp",EDGE,"E24.bottom")])]}),"instanceName":"1"});
            var sketch = newSketch(context, id + "F53", { "sketchPlane" : qUnion([Q0])});
            skLineSegment(sketch, "E33.bottom", {"start": v(55, -1405) * mm, "end": v(-505, -1405) * mm});
            skLineSegment(sketch, "E33.top", {"start": v(55, -1905) * mm, "end": v(-505, -1905) * mm});
            skLineSegment(sketch, "E33.left", {"start": v(55, -1405) * mm, "end": v(55, -1905) * mm});
            skLineSegment(sketch, "E33.right", {"start": v(-505, -1405) * mm, "end": v(-505, -1905) * mm});
            skSolve(sketch);
        }
        {
            var Q0;
            Q0 = qSketchRegion(id + "F53", true);
            extrude(context, id + "F54", {"entities" : qUnion([Q0]), "oppositeDirection" : true, "depth" : 514 * mm, "offsetDistance" : 25 * mm});
        }
        {
            var Q0;
            Q0=makeQuery(id+"F54.opExtrude","CAP_FACE",FACE,{"disambiguationData":[OSD([sQuery(id+"F53.wireOp",EDGE,"E33.bottom"),sQuery(id+"F53.wireOp",EDGE,"E33.top"),sQuery(id+"F53.wireOp",EDGE,"E33.left"),sQuery(id+"F53.wireOp",EDGE,"E33.right")])],"isStart":false});
            var sketch = newSketch(context, id + "F55", { "sketchPlane" : qUnion([Q0])});
            skLineSegment(sketch, "E34.bottom", {"start": v(-455, 1855) * mm, "end": v(5, 1855) * mm});
            skLineSegment(sketch, "E34.top", {"start": v(-455, 1455) * mm, "end": v(5, 1455) * mm});
            skLineSegment(sketch, "E34.left", {"start": v(-455, 1855) * mm, "end": v(-455, 1455) * mm});
            skLineSegment(sketch, "E34.right", {"start": v(5, 1855) * mm, "end": v(5, 1455) * mm});
            skSolve(sketch);
        }
        {
            var Q0;
            Q0 = qSketchRegion(id + "F55", true);
            extrude(context, id + "F56", {"entities" : qUnion([Q0]), "operationType" : NewBodyOperationType.REMOVE, "oppositeDirection" : true, "depth" : 490 * mm, "offsetDistance" : 25 * mm});
        }
    });
